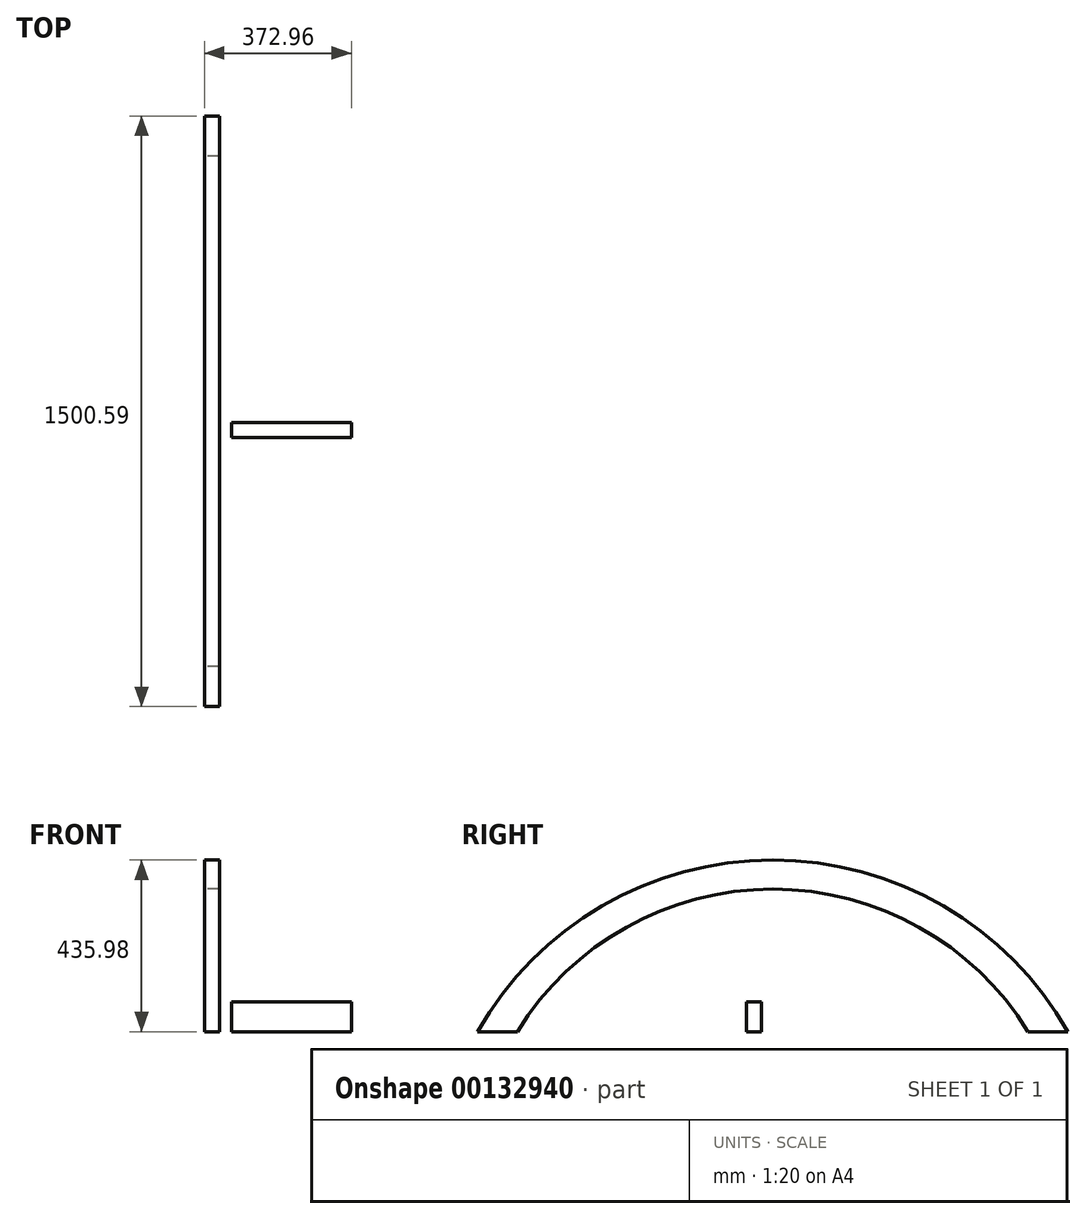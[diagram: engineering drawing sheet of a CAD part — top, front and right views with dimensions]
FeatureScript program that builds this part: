
annotation { "Feature Type Name" : "Feature", "Feature Type Description" : "" }
export const myFeature = defineFeature(function(context is Context, id is Id, definition is map)
    precondition{}
    {
        {
            var Q0;
            Q0=qCreatedBy(makeId("Right.planeOp"),FACE);
            var sketch = newSketch(context, id + "F0", { "sketchPlane" : qUnion([Q0])});
            skArc(sketch, "E0", {"start": v(677.02, 0) * mm, "mid": v(28.33, 362.2) * mm, "end": v(-620.37, 0) * mm});
            skLineSegment(sketch, "E1", {"start": v(-620.37, 0) * mm, "end": v(-721.97, 0) * mm});
            skLineSegment(sketch, "E2", {"start": v(677.02, 0) * mm, "end": v(778.62, 0) * mm});
            skArc(sketch, "E3", {"start": v(778.62, 0) * mm, "mid": v(28.33, 435.98) * mm, "end": v(-721.97, 0) * mm});
            skSolve(sketch);
        }
        {
            var Q0;
            Q0 = qSketchRegion(id + "F0", true);
            extrude(context, id + "F1", {"entities" : qUnion([Q0]), "depth" : 38.1 * mm});
        }
        {
            var Q0;
            Q0=qCreatedBy(makeId("Front.planeOp"),FACE);
            var sketch = newSketch(context, id + "F2", { "sketchPlane" : qUnion([Q0])});
            skLineSegment(sketch, "E4", {"start": v(68.16, 0) * mm, "end": v(68.16, 76.2) * mm});
            skLineSegment(sketch, "E5", {"start": v(68.16, 76.2) * mm, "end": v(372.96, 76.2) * mm});
            skLineSegment(sketch, "E6", {"start": v(372.96, 76.2) * mm, "end": v(372.96, 0) * mm});
            skLineSegment(sketch, "E7", {"start": v(372.96, 0) * mm, "end": v(68.16, 0) * mm});
            skSolve(sketch);
        }
        {
            var Q0;
            Q0=makeQuery(id+"F2.imprint","IMPRINT",FACE,{"disambiguationData":[TD([[makeQuery(id+"F2.imprint","IMPRINT",EDGE,{"derivedFrom":sQuery(id+"F2.wireOp",EDGE,"E4")}),-1.0]])]});
            extrude(context, id + "F3", {"entities" : qUnion([Q0]), "depth" : 38.1 * mm});
        }
    });
